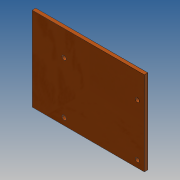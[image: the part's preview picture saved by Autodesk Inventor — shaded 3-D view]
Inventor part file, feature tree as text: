
AUTODESK INVENTOR PART (.ipt)
format: ipt  version: 2017 (Build 210142000, 142)  size: 97,280 bytes
history: native  units: mm
features: other x1, extrude x1, sketch x1
ambient origin geometry x8: Origin, YZ Plane, XZ Plane, XY Plane, X Axis, Y Axis, Z Axis, Center Point
bodies: Body1 (feature_tree)
feature tree (3):
  other  "Sólido1"
  extrude  "Extrusión1"  Depth=60.0mm
  sketch  "Boceto1"  dims[d0=3.0mm d1=60.0mm d2=18.0mm d3=2.5mm d4=0.0mm d5=96.0mm d6=20.0mm d7=15.0mm d8=5.0mm d9=55.0mm]
